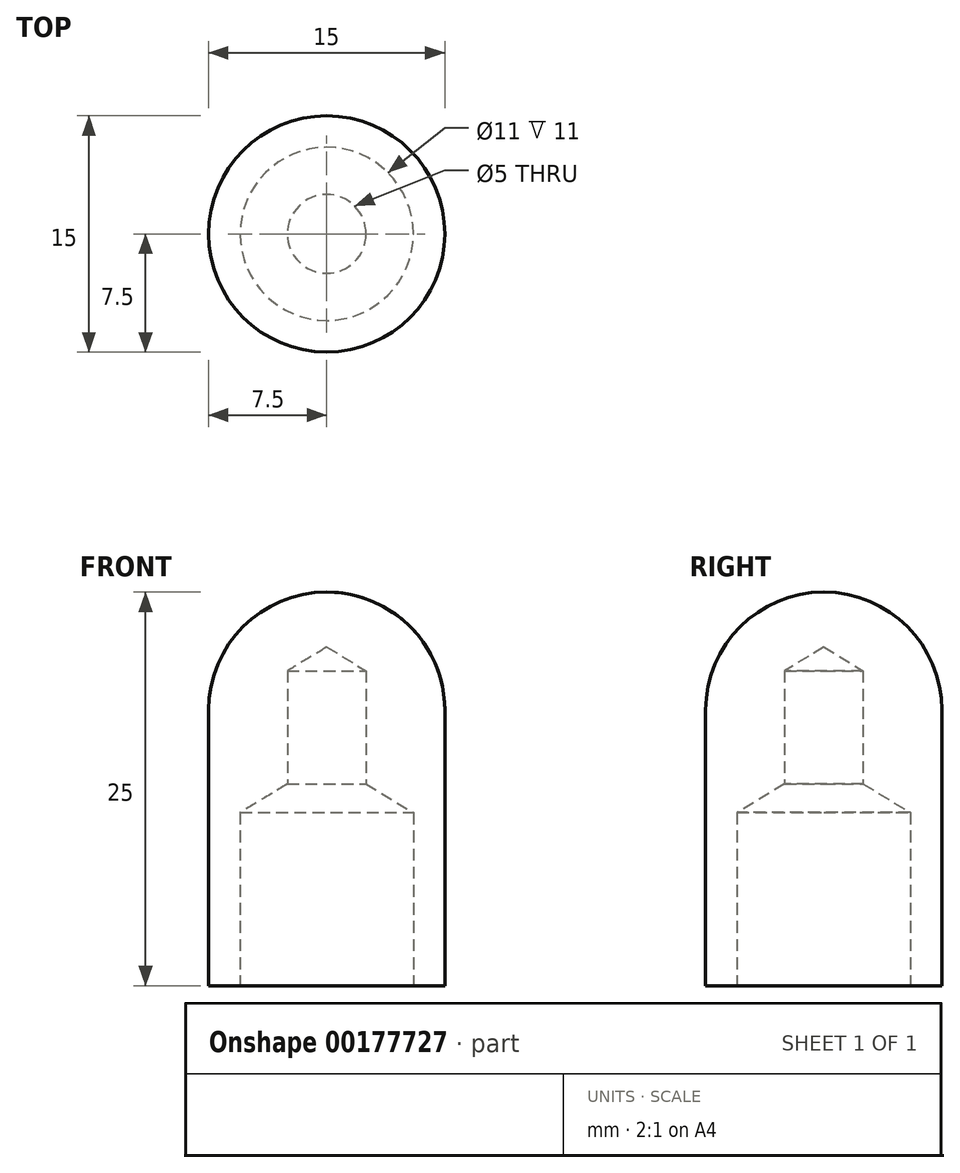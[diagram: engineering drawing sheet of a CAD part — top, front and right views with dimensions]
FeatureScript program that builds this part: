
annotation { "Feature Type Name" : "Feature", "Feature Type Description" : "" }
export const myFeature = defineFeature(function(context is Context, id is Id, definition is map)
    precondition{}
    {
        {
            var Q0;
            Q0=qCreatedBy(makeId("Top.planeOp"),FACE);
            var sketch = newSketch(context, id + "F0", { "sketchPlane" : qUnion([Q0])});
            skCircle(sketch, "E0", {"center": v(0, 0) * mm, "radius": 7.5 * mm});
            skSolve(sketch);
        }
        {
            var Q0;
            Q0=makeQuery(id+"F0.imprint","IMPRINT",FACE,{"disambiguationData":[TD([[makeQuery(id+"F0.imprint","IMPRINT",EDGE,{"derivedFrom":sQuery(id+"F0.wireOp",EDGE,"E0")}),1.0]])]});
            extrude(context, id + "F1", {"entities" : qUnion([Q0]), "depth" : 25 * mm});
        }
        {
            var Q0;
            Q0=makeQuery(id+"F1.opExtrude","CAP_FACE",FACE,{"disambiguationData":[OSD([sQuery(id+"F0.wireOp",EDGE,"E0")])],"isStart":true});
            var sketch = newSketch(context, id + "F2", { "sketchPlane" : qUnion([Q0])});
            skCircle(sketch, "E1", {"center": v(0, 0) * mm, "radius": 2.5 * mm});
            skSolve(sketch);
        }
        {
            var Q0;
            Q0=sQuery(id+"F2.wireOp",VERTEX,"E1.center");
            var Q1;
            Q1=makeQuery(id+"F1.opExtrude","SWEPT_BODY",BODY,{"disambiguationData":[OSD([sQuery(id+"F0.wireOp",EDGE,"E0")])]});
            hole(context, id + "F3", {"style" : HoleStyle.SIMPLE, "endStyle" : HoleEndStyle.BLIND, "holeDiameter" : 5 * mm, "holeDepth" : 20 * mm, "startFromSketch" : true, "locations" : qUnion([Q0]), "scope" : qUnion([Q1])});
        }
        {
            var Q0;
            Q0=makeQuery(id+"F1.opExtrude","CAP_FACE",FACE,{"disambiguationData":[OSD([sQuery(id+"F0.wireOp",EDGE,"E0")])],"isStart":true});
            var sketch = newSketch(context, id + "F4", { "sketchPlane" : qUnion([Q0])});
            skCircle(sketch, "E2", {"center": v(0, 0) * mm, "radius": 6 * mm});
            skSolve(sketch);
        }
        {
            var Q0;
            Q0=sQuery(id+"F4.wireOp",VERTEX,"E2.center");
            var Q1;
            Q1=makeQuery(id+"F1.opExtrude","SWEPT_BODY",BODY,{"disambiguationData":[OSD([sQuery(id+"F0.wireOp",EDGE,"E0")])]});
            hole(context, id + "F5", {"style" : HoleStyle.SIMPLE, "endStyle" : HoleEndStyle.BLIND, "holeDiameter" : 11 * mm, "holeDepth" : 11 * mm, "startFromSketch" : true, "locations" : qUnion([Q0]), "scope" : qUnion([Q1])});
        }
        {
            var Q0;
            Q0=makeQuery(id+"F1.opExtrude","CAP_EDGE",EDGE,{"disambiguationData":[OSD([sQuery(id+"F0.wireOp",EDGE,"E0")])],"isStart":false});
            fillet(context, id + "F6", {"entities" : qUnion([Q0]), "radius" : 7.5 * mm, "tangentPropagation" : true, "allowEdgeOverflow" : false});
        }
    });
